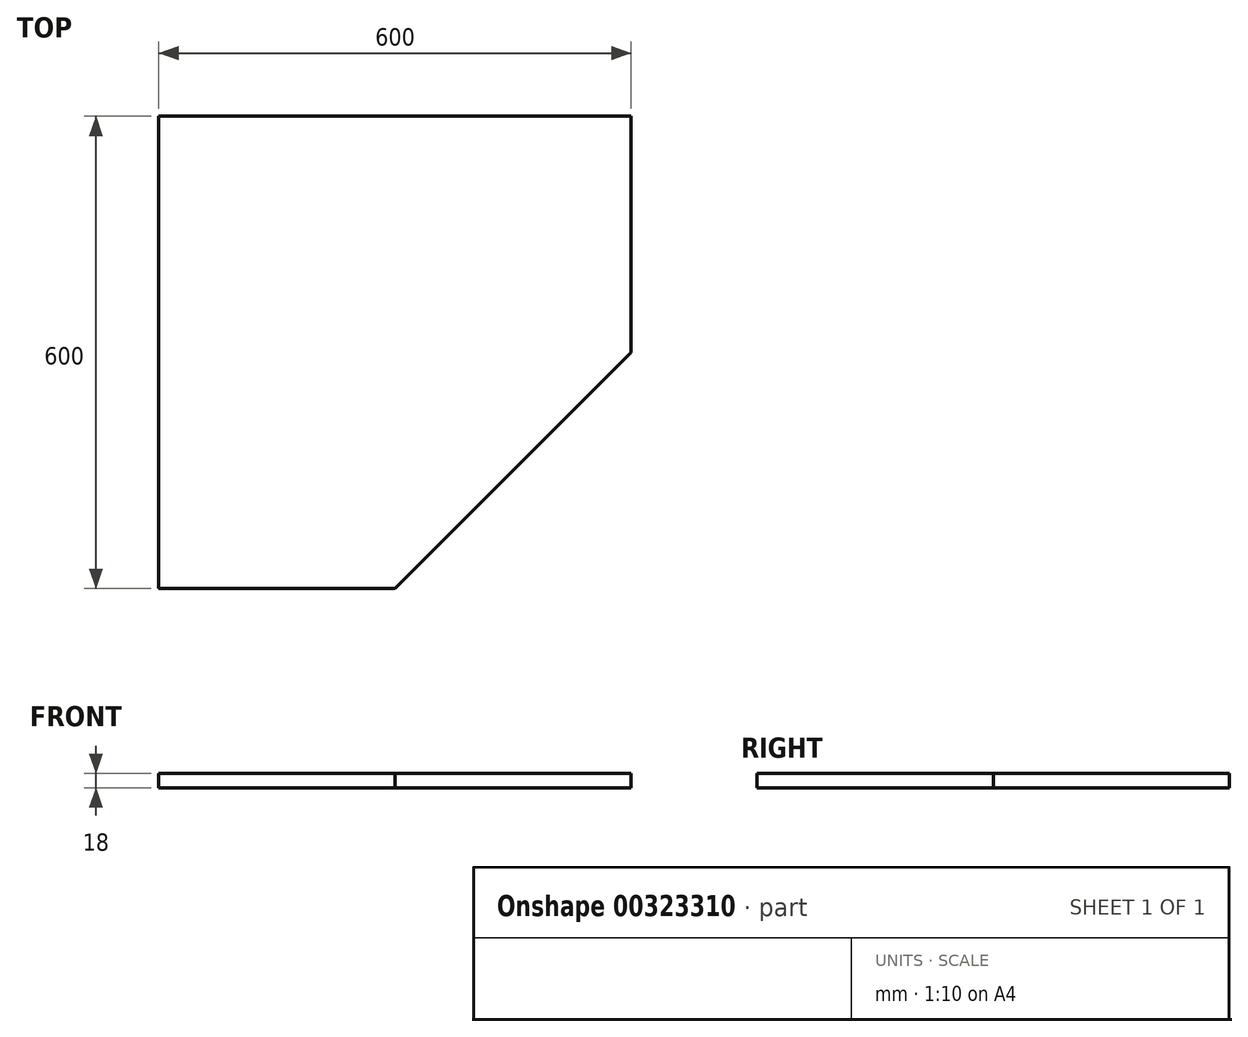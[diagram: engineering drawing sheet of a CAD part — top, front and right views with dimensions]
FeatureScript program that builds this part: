
annotation { "Feature Type Name" : "Feature", "Feature Type Description" : "" }
export const myFeature = defineFeature(function(context is Context, id is Id, definition is map)
    precondition{}
    {
        {
            var Q0;
            Q0=qCreatedBy(makeId("Top.planeOp"),FACE);
            var sketch = newSketch(context, id + "F0", { "sketchPlane" : qUnion([Q0])});
            skLineSegment(sketch, "E0.bottom", {"start": v(0, 0) * mm, "end": v(600, 0) * mm});
            skLineSegment(sketch, "E0.top", {"start": v(0, -600) * mm, "end": v(300, -600) * mm});
            skLineSegment(sketch, "E0.left", {"start": v(0, 0) * mm, "end": v(0, -600) * mm});
            skLineSegment(sketch, "E0.right", {"start": v(600, 0) * mm, "end": v(600, -300) * mm});
            skLineSegment(sketch, "E1", {"start": v(300, -600) * mm, "end": v(600, -300) * mm});
            skSolve(sketch);
        }
        {
            var Q0;
            Q0 = qSketchRegion(id + "F0", true);
            extrude(context, id + "F1", {"entities" : qUnion([Q0]), "depth" : 18 * mm, "offsetDistance" : 25 * mm});
        }
    });
